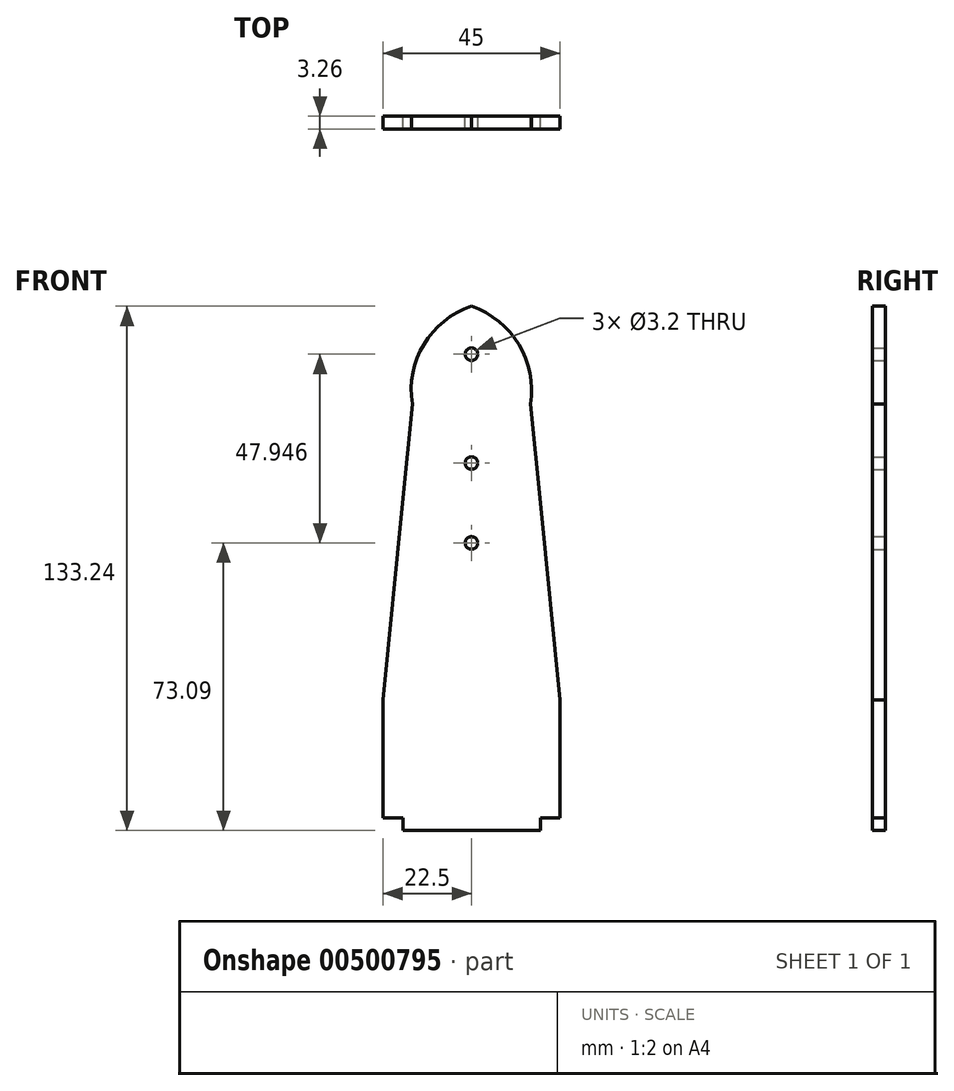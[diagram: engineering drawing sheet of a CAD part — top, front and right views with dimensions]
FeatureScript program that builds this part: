
annotation { "Feature Type Name" : "Feature", "Feature Type Description" : "" }
export const myFeature = defineFeature(function(context is Context, id is Id, definition is map)
    precondition{}
    {
        {
            var Q0;
            Q0=qCreatedBy(makeId("Front.planeOp"),FACE);
            var sketch = newSketch(context, id + "F0", { "sketchPlane" : qUnion([Q0])});
            skLineSegment(sketch, "E0", {"start": v(0, 0) * mm, "end": v(0, 100) * mm});
            skPoint(sketch, "E1.startSnap0", {"position": v(0, 50) * mm});
            skPoint(sketch, "E1.endSnap0", {"position": v(0, 50) * mm});
            skLineSegment(sketch, "E2", {"start": v(0, 50) * mm, "end": v(-17.5, 50) * mm});
            skLineSegment(sketch, "E3", {"start": v(0, 50) * mm, "end": v(17.5, 50) * mm});
            skLineSegment(sketch, "E4", {"start": v(-22.5, 0) * mm, "end": v(-17.5, 50) * mm});
            skLineSegment(sketch, "E5", {"start": v(22.5, 0) * mm, "end": v(17.5, 50) * mm});
            skLineSegment(sketch, "E6", {"start": v(0, 50) * mm, "end": v(0, 75.1) * mm});
            skLineSegment(sketch, "E7", {"start": v(0, 75.1) * mm, "end": v(-15, 75.1) * mm});
            skLineSegment(sketch, "E8", {"start": v(0, 75.1) * mm, "end": v(15, 75.1) * mm});
            skLineSegment(sketch, "E9", {"start": v(-17.5, 50) * mm, "end": v(-15, 75.1) * mm});
            skLineSegment(sketch, "E10", {"start": v(17.5, 50) * mm, "end": v(15, 75.1) * mm});
            skArc(sketch, "E11", {"start": v(0, 100) * mm, "mid": v(-12.08, 90.32) * mm, "end": v(-15, 75.1) * mm});
            skArc(sketch, "E12", {"start": v(15, 75.1) * mm, "mid": v(12.02, 90.28) * mm, "end": v(0, 100) * mm});
            skLineSegment(sketch, "E13", {"start": v(0, 75.1) * mm, "end": v(0, 87.8) * mm});
            skCircle(sketch, "E14", {"center": v(0, 87.8) * mm, "radius": 1.6 * mm});
            skLineSegment(sketch, "E15", {"start": v(-22.5, -30) * mm, "end": v(-17.45, -30) * mm});
            skLineSegment(sketch, "E16", {"start": v(22.6, -30) * mm, "end": v(17.55, -30) * mm});
            skLineSegment(sketch, "E17", {"start": v(-17.45, -30) * mm, "end": v(-17.45, -33.24) * mm});
            skLineSegment(sketch, "E18", {"start": v(17.55, -30) * mm, "end": v(17.55, -33.24) * mm});
            skLineSegment(sketch, "E19", {"start": v(-17.45, -33.24) * mm, "end": v(17.55, -33.24) * mm});
            skLineSegment(sketch, "E20.bottom", {"start": v(3.46, 60.15) * mm, "end": v(-3.46, 60.15) * mm});
            skLineSegment(sketch, "E20.top", {"start": v(3.46, 39.85) * mm, "end": v(-3.46, 39.85) * mm});
            skLineSegment(sketch, "E20.left", {"start": v(3.46, 60.15) * mm, "end": v(3.46, 39.85) * mm});
            skLineSegment(sketch, "E20.right", {"start": v(-3.46, 60.15) * mm, "end": v(-3.46, 39.85) * mm});
            skPoint(sketch, "E21", {"position": v(0, 60.15) * mm});
            skPoint(sketch, "E22", {"position": v(0, 39.85) * mm});
            skCircle(sketch, "E23", {"center": v(0, 39.85) * mm, "radius": 1.6 * mm});
            skCircle(sketch, "E24", {"center": v(0, 60.15) * mm, "radius": 1.6 * mm});
            skLineSegment(sketch, "E25", {"start": v(22.5, 0) * mm, "end": v(22.5, -30) * mm});
            skLineSegment(sketch, "E26", {"start": v(-22.5, 0) * mm, "end": v(-22.5, -30) * mm});
            skLineSegment(sketch, "E27", {"start": v(17.55, -30) * mm, "end": v(-17.45, -30) * mm});
            skSolve(sketch);
        }
        {
            var Q0;
            {var subQ0=sQuery(id+"F0.wireOp",EDGE,"E5");Q0=makeQuery(id+"F0.imprint","IMPRINT",FACE,{"disambiguationData":[TD([[makeQuery(id+"F0.imprint","IMPRINT",EDGE,{"derivedFrom":subQ0}),1.0]])]});}
            var Q1;
            {var subQ0=sQuery(id+"F0.wireOp",EDGE,"E4");Q1=makeQuery(id+"F0.imprint","IMPRINT",FACE,{"disambiguationData":[TD([[makeQuery(id+"F0.imprint","IMPRINT",EDGE,{"derivedFrom":subQ0}),-1.0]])]});}
            var Q2;
            {var subQ3=sQuery(id+"F0.wireOp",EDGE,"E17");Q2=makeQuery(id+"F0.imprint","IMPRINT",FACE,{"disambiguationData":[TD([[makeQuery(id+"F0.imprint","IMPRINT",EDGE,{"derivedFrom":subQ3}),1.0]])]});}
            var Q3;
            {var subQ1=sQuery(id+"F0.wireOp",EDGE,"E8");Q3=makeQuery(id+"F0.imprint","IMPRINT",FACE,{"disambiguationData":[TD([[makeQuery(id+"F0.imprint","IMPRINT",EDGE,{"derivedFrom":subQ1}),-1.0]])]});}
            var Q4;
            {var subQ1=sQuery(id+"F0.wireOp",EDGE,"E7");Q4=makeQuery(id+"F0.imprint","IMPRINT",FACE,{"disambiguationData":[TD([[makeQuery(id+"F0.imprint","IMPRINT",EDGE,{"derivedFrom":subQ1}),1.0]])]});}
            var Q5;
            {var subQ2=sQuery(id+"F0.wireOp",EDGE,"E8");Q5=makeQuery(id+"F0.imprint","IMPRINT",FACE,{"disambiguationData":[TD([[makeQuery(id+"F0.imprint","IMPRINT",EDGE,{"derivedFrom":subQ2}),1.0]])]});}
            var Q6;
            {var subQ1=sQuery(id+"F0.wireOp",EDGE,"E7");Q6=makeQuery(id+"F0.imprint","IMPRINT",FACE,{"disambiguationData":[TD([[makeQuery(id+"F0.imprint","IMPRINT",EDGE,{"derivedFrom":subQ1}),-1.0]])]});}
            var Q7;
            {var subQ0=sQuery(id+"F0.wireOp",EDGE,"E20.left");var subQ1=sQuery(id+"F0.wireOp",EDGE,"E20.bottom");var subQ2=makeQuery(id+"F0.imprint","INTERSECT",VERTEX,{"derivedFrom":[subQ1,subQ0]});Q7=makeQuery(id+"F0.imprint","IMPRINT",FACE,{"disambiguationData":[TD([[makeQuery(id+"F0.imprint","IMPRINT",EDGE,{"disambiguationData":[TD([[subQ2,-1.0]])],"derivedFrom":subQ1}),1.0]])]});}
            var Q8;
            {var subQ0=sQuery(id+"F0.wireOp",EDGE,"E20.right");var subQ1=sQuery(id+"F0.wireOp",EDGE,"E20.bottom");var subQ2=makeQuery(id+"F0.imprint","INTERSECT",VERTEX,{"derivedFrom":[subQ1,subQ0]});Q8=makeQuery(id+"F0.imprint","IMPRINT",FACE,{"disambiguationData":[TD([[makeQuery(id+"F0.imprint","IMPRINT",EDGE,{"disambiguationData":[TD([[subQ2,1.0]])],"derivedFrom":subQ1}),1.0]])]});}
            var Q9;
            {var subQ0=sQuery(id+"F0.wireOp",EDGE,"E20.right");var subQ1=sQuery(id+"F0.wireOp",EDGE,"E20.top");var subQ2=makeQuery(id+"F0.imprint","INTERSECT",VERTEX,{"derivedFrom":[subQ1,subQ0]});Q9=makeQuery(id+"F0.imprint","IMPRINT",FACE,{"disambiguationData":[TD([[makeQuery(id+"F0.imprint","IMPRINT",EDGE,{"disambiguationData":[TD([[subQ2,1.0]])],"derivedFrom":subQ1}),-1.0]])]});}
            var Q10;
            {var subQ0=sQuery(id+"F0.wireOp",EDGE,"E20.left");var subQ1=sQuery(id+"F0.wireOp",EDGE,"E20.top");var subQ2=makeQuery(id+"F0.imprint","INTERSECT",VERTEX,{"derivedFrom":[subQ1,subQ0]});Q10=makeQuery(id+"F0.imprint","IMPRINT",FACE,{"disambiguationData":[TD([[makeQuery(id+"F0.imprint","IMPRINT",EDGE,{"disambiguationData":[TD([[subQ2,-1.0]])],"derivedFrom":subQ1}),-1.0]])]});}
            extrude(context, id + "F1", {"entities" : qUnion([Q0, Q1, Q2, Q3, Q4, Q5, Q6, Q7, Q8, Q9, Q10]), "depth" : 3.25 * mm, "offsetDistance" : 25 * mm, "symmetric" : true});
        }
    });
